FCSTD DOCUMENT  (FreeCAD 0.20R29410 (Git))
Label: #0_ASSEMBLY_ELECTROMAGNET
License: All rights reserved
LicenseURL: http://en.wikipedia.org/wiki/All_rights_reserved
objects: App::FeaturePython×4, Part::FeaturePython×3, Mesh::Feature×2, Sketcher::SketchObject×1, PartDesign::Pad×1, PartDesign::Body×1
note: 7 computed .brp shape members not serialized (recipe doc carries the construction recipe); baked Part::Feature solids carry a one-line shape summary decoded from their .brp

FEATURE [Sketcher::SketchObject] Sketch
  FullyConstrained = false
  MapMode = 5
  Support = -> [XY_Plane]
  sketch-geometry (1):
    g0: Circle CenterX=0 CenterY=0 CenterZ=0 NormalX=0 NormalY=0 NormalZ=1 AngleXU=0 Radius=12.6073
  constraints (1):
    c: Coincident(g0,g-1)
FEATURE [PartDesign::Pad] Pad
  Direction = (0,0,1)
  Length = 10
  Length2 = 10
  Profile = -> Sketch
  ReferenceAxis = -> Sketch [N_Axis]
  Refine = true
  Reversed = true
  Type = 0
FEATURE [PartDesign::Body] Body
  Group = -> [Sketch,Pad]
  Origin = -> Origin
  Tip = -> Pad
FEATURE [Part::FeaturePython] Body_001  # a2plus imported part (geometry in sourceFile) (typed FeaturePython)
  a2p_Version = 0.4.60n
  fixedPosition = true
  localSourceObject = Body
  objectType = a2pPart
  sourceFile = converted
  subassemblyImport = false
  timeLastImport = 1.68934e+09
  updateColors = true
FEATURE [Part::FeaturePython] b__23_TOOL_Electromagnet_001_  label="#23_TOOL_Electromagnet_001"  # a2plus imported part (geometry in sourceFile) (typed FeaturePython)
  Placement = pos=(14.52,14,-7.5) rot=(0,1,0;3.14159rad)
  a2p_Version = 0.4.60n
  fixedPosition = false
  objectType = a2pPart
  sourceFile = ./#23_TOOL_Electromagnet.FCStd
  subassemblyImport = false
  timeLastImport = 1.68925e+09
  updateColors = true
FEATURE [App::FeaturePython] circularEdge_001  label="circularEdge_001__Body_001"  # a2plus constraint (typed FeaturePython)
  Object1 = b__23_TOOL_Electromagnet_001_
  Object2 = Body_001
  ParentTreeObject = -> b__23_TOOL_Electromagnet_001_
  SubElement1 = Edge23
  SubElement2 = Edge2
  Suppressed = false
  Type = circularEdge
  directionConstraint = 0
  lockRotation = false
  offset = 0
FEATURE [App::FeaturePython] circularEdge_001_mirror  label="circularEdge_001__#23_TOOL_Electromagnet_001"  # a2plus constraint (typed FeaturePython)
  Object1 = b__23_TOOL_Electromagnet_001_
  Object2 = Body_001
  ParentTreeObject = -> Body_001
  SubElement1 = Edge23
  SubElement2 = Edge2
  Suppressed = false
  Type = circularEdge
  directionConstraint = 0
  lockRotation = false
  offset = 0
FEATURE [Part::FeaturePython] b_electromagnet1_001_  label="electromagnet1_001"  # a2plus imported part (geometry in sourceFile) (typed FeaturePython)
  Placement = pos=(-20.3334,-22.3135,20) rot=(0,0,1;0rad)
  a2p_Version = 0.4.60n
  fixedPosition = false
  objectType = a2pPart
  sourceFile = ./../Complements/electromagnet.step
  subassemblyImport = false
  timeLastImport = 1.68907e+09
  updateColors = true
FEATURE [App::FeaturePython] circularEdge_002  label="circularEdge_002__#23_TOOL_Electromagnet_001"  # a2plus constraint (typed FeaturePython)
  Object1 = b_electromagnet1_001_
  Object2 = b__23_TOOL_Electromagnet_001_
  ParentTreeObject = -> b_electromagnet1_001_
  SubElement1 = Edge100
  SubElement2 = Edge27
  Suppressed = false
  Type = circularEdge
  directionConstraint = 1
  lockRotation = false
  offset = 0
FEATURE [App::FeaturePython] circularEdge_002_mirror  label="circularEdge_002__electromagnet1_001"  # a2plus constraint (typed FeaturePython)
  Object1 = b_electromagnet1_001_
  Object2 = b__23_TOOL_Electromagnet_001_
  ParentTreeObject = -> b__23_TOOL_Electromagnet_001_
  SubElement1 = Edge100
  SubElement2 = Edge27
  Suppressed = false
  Type = circularEdge
  directionConstraint = 1
  lockRotation = false
  offset = 0
FEATURE [Mesh::Feature] Mesh  label="#23_TOOL_Electromagnet_001 (Meshed)"
FEATURE [Mesh::Feature] Mesh001  label="electromagnet1_001 (Meshed)"
